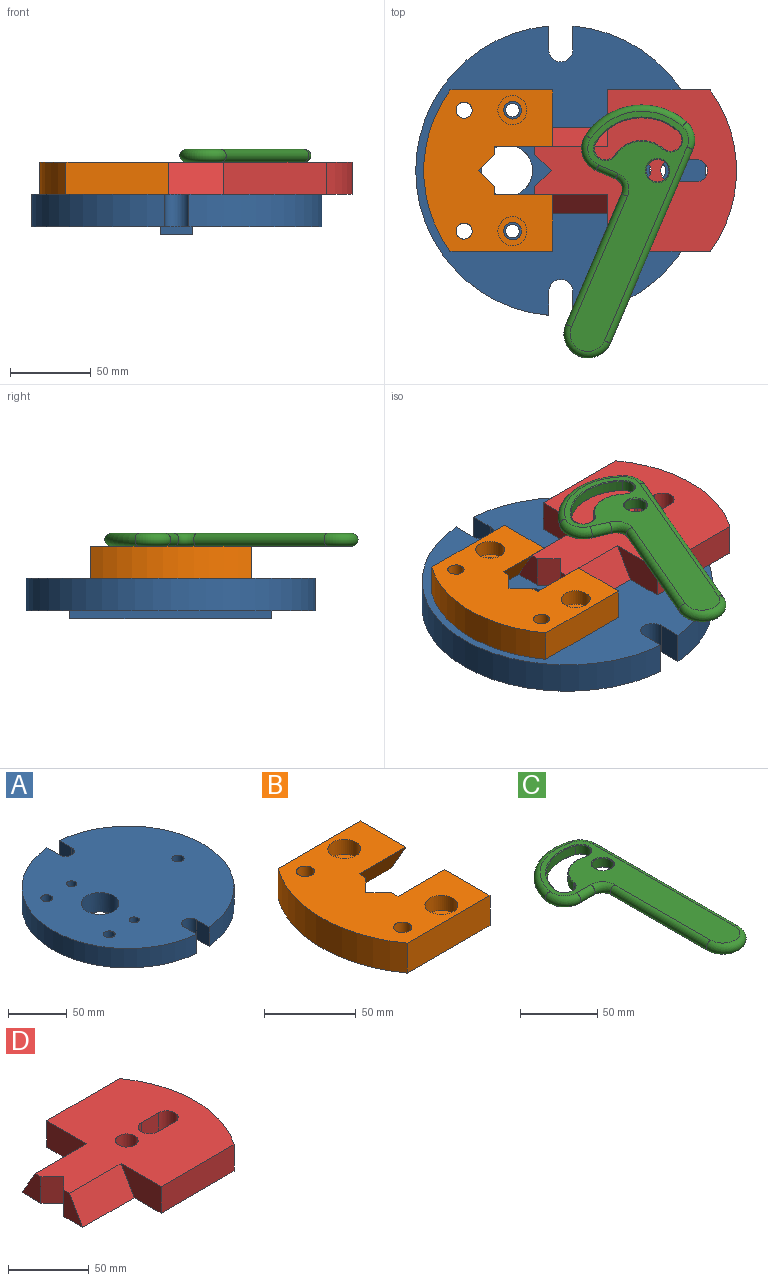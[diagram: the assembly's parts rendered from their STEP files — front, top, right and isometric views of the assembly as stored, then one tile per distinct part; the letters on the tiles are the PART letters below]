
ASSEMBLY  parts=4 mates=7
PART A: 21 faces, bbox 180x179.4x25 mm
  f0: plane 180x179.37mm, normal (0,0,-1), area 21165.2mm2, adj f1,f2,f3,f4,f5,f7,f8,f9
  f1: cylinder r=90mm len=179.37mm, axis (0,0,-1), area 5354.5mm2, adj f0,f2,f6,f13
  f2: plane 20x14.69mm, normal (-1,0,0), area 293.7mm2, adj f0,f1,f3,f6
  f3: cylinder r=7.5mm len=20mm, axis (0,0,-1), area 471.2mm2, adj f0,f2,f4,f6
  f4: plane 20x14.69mm, normal (1,0,0), area 293.7mm2, adj f0,f3,f5,f6
  f5: cylinder r=90mm len=179.37mm, axis (0,0,-1), area 5354.5mm2, adj f0,f4,f6,f15
  f6: plane 180x179.37mm, normal (0,0,1), area 23665.2mm2, adj f1,f2,f3,f4,f5,f11,f12,f13
  f7: plane 125x5mm, normal (-1,0,0), area 625mm2, adj f0,f9,f10,f16
  f8: plane 125x5mm, normal (1,0,0), area 625mm2, adj f0,f9,f10,f16
  f9: plane 20x5mm, normal (0,1,0), area 100mm2, adj f0,f7,f8,f10
  f10: plane 125x20mm, normal (0,0,-1), area 2500mm2, adj f7,f8,f9,f16
  f11: cylinder r=5mm len=20mm, axis (0,0,-1), area 628.3mm2, adj f0,f6
  f12: cylinder r=4.25mm len=20mm, axis (0,0,-1), area 534.1mm2, adj f0,f6
  f13: plane 20x14.69mm, normal (-1,0,0), area 293.7mm2, adj f0,f1,f6,f14
  f14: cylinder r=7.5mm len=20mm, axis (0,0,-1), area 471.2mm2, adj f0,f6,f13,f15
  f15: plane 20x14.69mm, normal (1,0,0), area 293.7mm2, adj f0,f5,f6,f14
  f16: plane 20x5mm, normal (0,-1,0), area 100mm2, adj f0,f7,f8,f10
  f17: cylinder r=5mm len=20mm, axis (0,0,-1), area 628.3mm2, adj f0,f6
  f18: cylinder r=4.25mm len=20mm, axis (0,0,-1), area 534.1mm2, adj f0,f6
  f19: cylinder r=16mm len=32mm, axis (0,0,-1), area 2010.6mm2, adj f0,f6
  f20: cylinder r=5.15mm len=20mm, axis (0,0,-1), area 647.2mm2, adj f0,f6
PART B: 21 faces, bbox 80x100x20 mm
  f0: plane 20x16.55mm, normal (1,0,0), area 215.5mm2, adj f1,f11,f13,f14
  f1: plane 20x10mm, normal (0.71,0.71,0), area 282.8mm2, adj f0,f2,f13,f14
  f2: plane 20x10mm, normal (0.71,-0.71,0), area 282.8mm2, adj f1,f3,f13,f14
  f3: plane 20x16.55mm, normal (1,0,0), area 215.5mm2, adj f2,f4,f13,f14
  f4: plane 36x20mm, normal (0,-0.87,-0.5), area 831.4mm2, adj f3,f5,f13,f14
  f5: plane 35x20mm, normal (1,0,0), area 584.5mm2, adj f4,f6,f13,f14
  f6: plane 63.74x20mm, normal (0,1,0), area 1274.8mm2, adj f5,f7,f13,f14
  f7: cylinder r=85mm len=100mm, axis (0,0,-1), area 2138.2mm2, adj f6,f8,f13,f14
  f8: plane 63.74x20mm, normal (0,-1,0), area 1274.8mm2, adj f7,f9,f13,f14
  f9: plane 35x20mm, normal (1,0,0), area 584.5mm2, adj f8,f11,f13,f14
  f10: cylinder r=5mm len=20mm, axis (0,0,-1), area 628.3mm2, adj f13,f14
  f11: plane 36x20mm, normal (0,0.87,-0.5), area 831.4mm2, adj f0,f9,f13,f14
  f12: cylinder r=5mm len=20mm, axis (0,0,-1), area 628.3mm2, adj f13,f14
  f13: plane 100x80mm, normal (0,0,1), area 5634.5mm2, adj f0,f1,f2,f3,f4,f5,f6,f7
  f14: plane 100x80mm, normal (0,0,-1), area 5122mm2, adj f0,f1,f2,f3,f4,f5,f6,f7
  f15: cylinder r=5.5mm len=11mm, axis (0,0,1), area 345.6mm2, adj f14,f16
  f16: plane 18x18mm, normal (0,0,1), area 159.4mm2, adj f15,f17
  f17: cylinder r=9mm len=18mm, axis (0,0,1), area 565.5mm2, adj f13,f16
  f18: cylinder r=5.5mm len=11mm, axis (0,0,1), area 345.6mm2, adj f14,f19
  f19: plane 18x18mm, normal (0,0,1), area 159.4mm2, adj f18,f20
  f20: cylinder r=9mm len=18mm, axis (0,0,1), area 565.5mm2, adj f13,f19
PART C: 25 faces, bbox 69.4x166.7x7.9 mm
  f0: cylinder r=7mm len=13.88mm, axis (0,0,-1), area 151.7mm2, adj f1,f4,f16,f21
  f1: cylinder r=34mm len=44.12mm, axis (0,0,-1), area 399.9mm2, adj f0,f2,f15,f20
  f2: cylinder r=7mm len=13.64mm, axis (0,0,-1), area 151.7mm2, adj f1,f4,f17,f22
  f3: cylinder r=7mm len=14mm, axis (0,0,-1), area 303.5mm2, adj f19,f24
  f4: cylinder r=20mm len=25.95mm, axis (0,0,-1), area 235.3mm2, adj f0,f2,f18,f23
  f5: plane 154.1x57.13mm, normal (0,0,1), area 3515.4mm2, adj f7,f8,f9,f10,f11,f12,f13,f14
  f6: plane 154.1x57.13mm, normal (0,0,-1), area 3515.4mm2, adj f7,f8,f9,f10,f11,f12,f13,f14
  f7: cylinder r=3.95mm len=88mm, axis (0,1,0), area 1092mm2, adj f5,f6,f8,f9
  f8: torus R=10.95mm, axis (0,0,1), area 164.4mm2, adj f5,f6,f7,f10
  f9: torus R=11.05mm, axis (0,0,1), area 528.8mm2, adj f5,f6,f7,f11
  f10: cylinder r=3.95mm len=13.03mm, axis (-1,0,0), area 161.7mm2, adj f5,f6,f8,f12
  f11: cylinder r=3.95mm len=130.63mm, axis (0,-1,0), area 1621mm2, adj f5,f6,f9,f13
  f12: torus R=11.05mm, axis (0,0,1), area 295.8mm2, adj f5,f6,f10,f14
  f13: torus R=11.05mm, axis (0,0,1), area 210.5mm2, adj f5,f6,f11,f14
  f14: torus R=38.05mm, axis (0,0,1), area 858.2mm2, adj f5,f6,f12,f13
  f15: cone r=34mm half-angle=45deg, axis (0,0,-1), area 41.3mm2, adj f1,f6,f16,f17
  f16: cone r=7mm half-angle=45deg, axis (0,0,-1), area 16.1mm2, adj f0,f6,f15,f18
  f17: cone r=7mm half-angle=45deg, axis (0,0,-1), area 16.1mm2, adj f2,f6,f15,f18
  f18: cone r=19.5mm half-angle=45deg, axis (0,0,1), area 23.8mm2, adj f4,f6,f16,f17
  f19: cone r=7.5mm half-angle=45deg, axis (0,0,-1), area 32.2mm2, adj f3,f6
  f20: cone r=34.5mm half-angle=45deg, axis (0,0,1), area 41.3mm2, adj f1,f5,f21,f22
  f21: cone r=7.5mm half-angle=45deg, axis (0,0,1), area 16.1mm2, adj f0,f5,f20,f23
  f22: cone r=7.5mm half-angle=45deg, axis (0,0,1), area 16.1mm2, adj f2,f5,f20,f23
  f23: cone r=20mm half-angle=45deg, axis (0,0,-1), area 23.8mm2, adj f4,f5,f21,f22
  f24: cone r=7mm half-angle=45deg, axis (0,0,1), area 32.2mm2, adj f3,f5
PART D: 18 faces, bbox 125x100x20 mm
  f0: plane 20x15mm, normal (0,-1,0), area 300mm2, adj f1,f15,f16,f17
  f1: cylinder r=7mm len=20mm, axis (0,0,-1), area 439.8mm2, adj f0,f2,f16,f17
  f2: plane 20x15mm, normal (0,1,0), area 300mm2, adj f1,f15,f16,f17
  f3: plane 45x20mm, normal (0,0.87,0.5), area 1039.2mm2, adj f4,f14,f16,f17
  f4: plane 20x16.55mm, normal (-1,0,0), area 215.5mm2, adj f3,f5,f16,f17
  f5: plane 20x10mm, normal (-0.71,-0.71,0), area 282.8mm2, adj f4,f6,f16,f17
  f6: plane 20x10mm, normal (-0.71,0.71,0), area 282.8mm2, adj f5,f7,f16,f17
  f7: plane 20x16.55mm, normal (-1,0,0), area 215.5mm2, adj f6,f8,f16,f17
  f8: plane 45x20mm, normal (0,-0.87,0.5), area 1039.2mm2, adj f7,f9,f16,f17
  f9: plane 35x20mm, normal (-1,0,0), area 584.5mm2, adj f8,f10,f16,f17
  f10: plane 63.74x20mm, normal (0,-1,0), area 1274.8mm2, adj f9,f11,f16,f17
  f11: cylinder r=85mm len=100mm, axis (0,0,-1), area 2138.2mm2, adj f10,f12,f16,f17
  f12: plane 63.74x20mm, normal (0,1,0), area 1274.8mm2, adj f11,f14,f16,f17
  f13: cylinder r=7mm len=20mm, axis (0,0,-1), area 879.6mm2, adj f16,f17
  f14: plane 35x20mm, normal (-1,0,0), area 584.5mm2, adj f3,f12,f16,f17
  f15: cylinder r=7mm len=20mm, axis (0,0,-1), area 439.8mm2, adj f0,f2,f16,f17
  f16: plane 125x100mm, normal (0,0,1), area 8212.7mm2, adj f0,f1,f2,f3,f4,f5,f6,f7
  f17: plane 125x100mm, normal (0,0,-1), area 9251.9mm2, adj f0,f1,f2,f3,f4,f5,f6,f7
PLACE A t=(-10.07,-16.39,-23.36)mm fixed
PLACE B t=(-10.07,-16.39,-23.36)mm
PLACE C rot(axis=(0,0,-1),23.1deg) t=(-5.27,7.13,-23.36)mm
PLACE D t=(14.87,-16.39,-23.36)mm
MATE planar D.f16 <-> C.f6  axis (0,0,1) through (47.41,-16.39,16.64)mm
MATE planar A.f6 <-> D.f17  axis (0,0,1) through (-8.6,-16.39,-3.36)mm
MATE revolute A.f12 <-> B.f18  axis (0,0,1) through (-40.07,21.11,-3.36)mm
MATE cylindrical C.f3 <-> A.f20  axis (0,0,-1) through (49.93,-16.39,24.04)mm
MATE planar B.f14 <-> A.f6  axis (0,0,-1) through (-59.82,-16.39,-3.36)mm
MATE planar B.f4 <-> D.f3  axis (0,-0.87,-0.5) through (-33.07,4.39,6.64)mm
MATE revolute A.f18 <-> B.f15  axis (0,0,1) through (-40.07,-53.89,-3.36)mm
